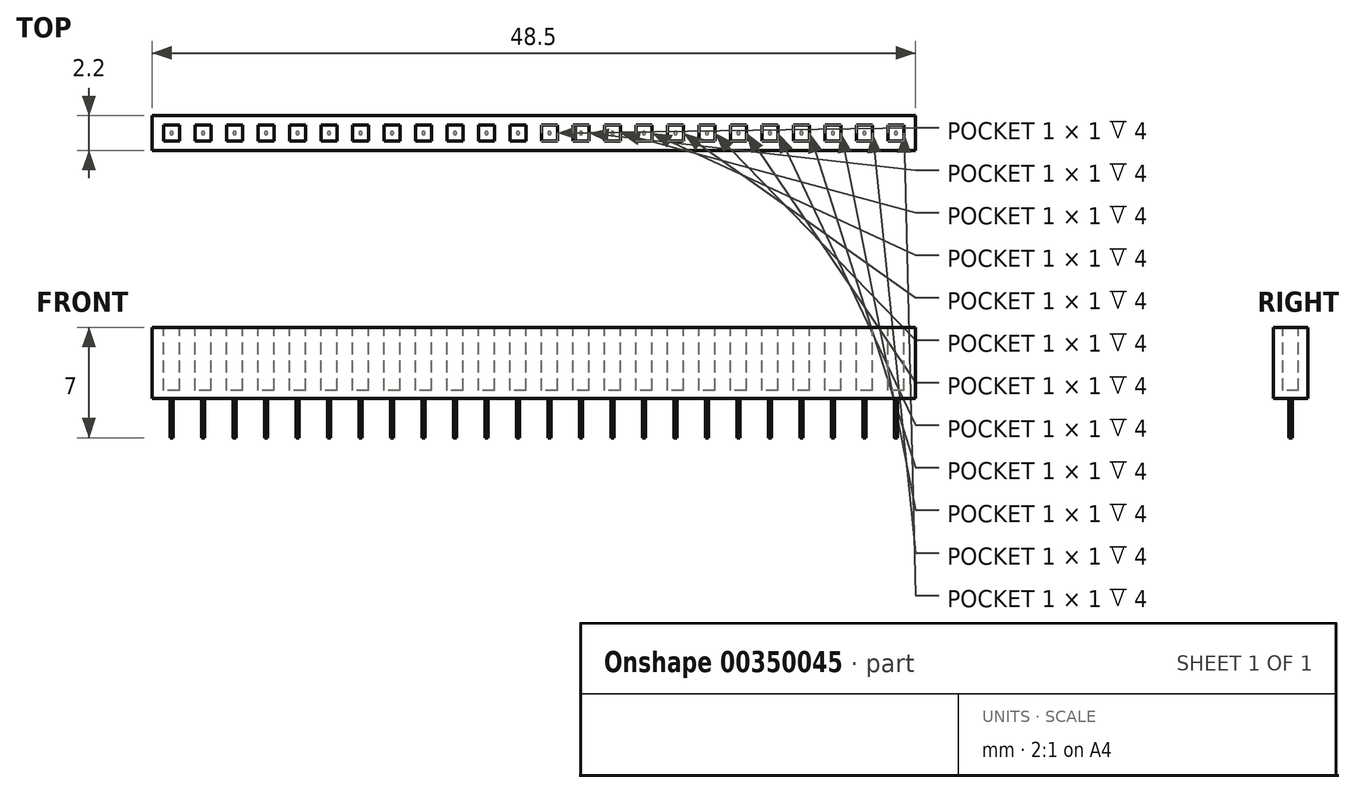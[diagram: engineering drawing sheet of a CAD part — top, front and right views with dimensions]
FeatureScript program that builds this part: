
annotation { "Feature Type Name" : "Feature", "Feature Type Description" : "" }
export const myFeature = defineFeature(function(context is Context, id is Id, definition is map)
    precondition{}
    {
        {
            var Q0;
            Q0=qCreatedBy(makeId("Top.planeOp"),FACE);
            var sketch = newSketch(context, id + "F0", { "sketchPlane" : qUnion([Q0])});
            skLineSegment(sketch, "E0.bottom", {"start": v(-24.25, 1.1) * mm, "end": v(24.25, 1.1) * mm});
            skLineSegment(sketch, "E0.top", {"start": v(-24.25, -1.1) * mm, "end": v(24.25, -1.1) * mm});
            skLineSegment(sketch, "E0.left", {"start": v(-24.25, 1.1) * mm, "end": v(-24.25, -1.1) * mm});
            skLineSegment(sketch, "E0.right", {"start": v(24.25, 1.1) * mm, "end": v(24.25, -1.1) * mm});
            skPoint(sketch, "E0.middle", {"position": v(0, 0) * mm});
            skSolve(sketch);
        }
        {
            var Q0;
            Q0=qSketchRegion(id+"F0",true);
            extrude(context, id + "F1", {"entities" : qUnion([Q0]), "depth" : 4.5 * mm});
        }
        {
            var Q0;
            Q0=makeQuery(id+"F1.opExtrude","CAP_FACE",FACE,{"disambiguationData":[OSD([sQuery(id+"F0.wireOp",EDGE,"E0.bottom"),sQuery(id+"F0.wireOp",EDGE,"E0.top"),sQuery(id+"F0.wireOp",EDGE,"E0.left"),sQuery(id+"F0.wireOp",EDGE,"E0.right")])],"isStart":false});
            var sketch = newSketch(context, id + "F2", { "sketchPlane" : qUnion([Q0])});
            skLineSegment(sketch, "E1.bottom", {"start": v(23.5, 0.5) * mm, "end": v(22.5, 0.5) * mm});
            skLineSegment(sketch, "E1.top", {"start": v(23.5, -0.5) * mm, "end": v(22.5, -0.5) * mm});
            skLineSegment(sketch, "E1.left", {"start": v(23.5, 0.5) * mm, "end": v(23.5, -0.5) * mm});
            skLineSegment(sketch, "E1.right", {"start": v(22.5, 0.5) * mm, "end": v(22.5, -0.5) * mm});
            skPoint(sketch, "E1.middle", {"position": v(23, 0) * mm});
            skLineSegment(sketch, "E2.1.0.0", {"start": v(21.5, 0.5) * mm, "end": v(20.5, 0.5) * mm});
            skLineSegment(sketch, "E2.1.0.1", {"start": v(21.5, -0.5) * mm, "end": v(20.5, -0.5) * mm});
            skLineSegment(sketch, "E2.1.0.2", {"start": v(21.5, 0.5) * mm, "end": v(21.5, -0.5) * mm});
            skLineSegment(sketch, "E2.1.0.3", {"start": v(20.5, 0.5) * mm, "end": v(20.5, -0.5) * mm});
            skLineSegment(sketch, "E2.2.0.0", {"start": v(19.5, 0.5) * mm, "end": v(18.5, 0.5) * mm});
            skLineSegment(sketch, "E2.2.0.1", {"start": v(19.5, -0.5) * mm, "end": v(18.5, -0.5) * mm});
            skLineSegment(sketch, "E2.2.0.2", {"start": v(19.5, 0.5) * mm, "end": v(19.5, -0.5) * mm});
            skLineSegment(sketch, "E2.2.0.3", {"start": v(18.5, 0.5) * mm, "end": v(18.5, -0.5) * mm});
            skLineSegment(sketch, "E2.3.0.0", {"start": v(17.5, 0.5) * mm, "end": v(16.5, 0.5) * mm});
            skLineSegment(sketch, "E2.3.0.1", {"start": v(17.5, -0.5) * mm, "end": v(16.5, -0.5) * mm});
            skLineSegment(sketch, "E2.3.0.2", {"start": v(17.5, 0.5) * mm, "end": v(17.5, -0.5) * mm});
            skLineSegment(sketch, "E2.3.0.3", {"start": v(16.5, 0.5) * mm, "end": v(16.5, -0.5) * mm});
            skLineSegment(sketch, "E2.4.0.0", {"start": v(15.5, 0.5) * mm, "end": v(14.5, 0.5) * mm});
            skLineSegment(sketch, "E2.4.0.1", {"start": v(15.5, -0.5) * mm, "end": v(14.5, -0.5) * mm});
            skLineSegment(sketch, "E2.4.0.2", {"start": v(15.5, 0.5) * mm, "end": v(15.5, -0.5) * mm});
            skLineSegment(sketch, "E2.4.0.3", {"start": v(14.5, 0.5) * mm, "end": v(14.5, -0.5) * mm});
            skLineSegment(sketch, "E2.5.0.0", {"start": v(13.5, 0.5) * mm, "end": v(12.5, 0.5) * mm});
            skLineSegment(sketch, "E2.5.0.1", {"start": v(13.5, -0.5) * mm, "end": v(12.5, -0.5) * mm});
            skLineSegment(sketch, "E2.5.0.2", {"start": v(13.5, 0.5) * mm, "end": v(13.5, -0.5) * mm});
            skLineSegment(sketch, "E2.5.0.3", {"start": v(12.5, 0.5) * mm, "end": v(12.5, -0.5) * mm});
            skLineSegment(sketch, "E2.6.0.0", {"start": v(11.5, 0.5) * mm, "end": v(10.5, 0.5) * mm});
            skLineSegment(sketch, "E2.6.0.1", {"start": v(11.5, -0.5) * mm, "end": v(10.5, -0.5) * mm});
            skLineSegment(sketch, "E2.6.0.2", {"start": v(11.5, 0.5) * mm, "end": v(11.5, -0.5) * mm});
            skLineSegment(sketch, "E2.6.0.3", {"start": v(10.5, 0.5) * mm, "end": v(10.5, -0.5) * mm});
            skLineSegment(sketch, "E2.7.0.0", {"start": v(9.5, 0.5) * mm, "end": v(8.5, 0.5) * mm});
            skLineSegment(sketch, "E2.7.0.1", {"start": v(9.5, -0.5) * mm, "end": v(8.5, -0.5) * mm});
            skLineSegment(sketch, "E2.7.0.2", {"start": v(9.5, 0.5) * mm, "end": v(9.5, -0.5) * mm});
            skLineSegment(sketch, "E2.7.0.3", {"start": v(8.5, 0.5) * mm, "end": v(8.5, -0.5) * mm});
            skLineSegment(sketch, "E2.8.0.0", {"start": v(7.5, 0.5) * mm, "end": v(6.5, 0.5) * mm});
            skLineSegment(sketch, "E2.8.0.1", {"start": v(7.5, -0.5) * mm, "end": v(6.5, -0.5) * mm});
            skLineSegment(sketch, "E2.8.0.2", {"start": v(7.5, 0.5) * mm, "end": v(7.5, -0.5) * mm});
            skLineSegment(sketch, "E2.8.0.3", {"start": v(6.5, 0.5) * mm, "end": v(6.5, -0.5) * mm});
            skLineSegment(sketch, "E2.9.0.0", {"start": v(5.5, 0.5) * mm, "end": v(4.5, 0.5) * mm});
            skLineSegment(sketch, "E2.9.0.1", {"start": v(5.5, -0.5) * mm, "end": v(4.5, -0.5) * mm});
            skLineSegment(sketch, "E2.9.0.2", {"start": v(5.5, 0.5) * mm, "end": v(5.5, -0.5) * mm});
            skLineSegment(sketch, "E2.9.0.3", {"start": v(4.5, 0.5) * mm, "end": v(4.5, -0.5) * mm});
            skLineSegment(sketch, "E2.10.0.0", {"start": v(3.5, 0.5) * mm, "end": v(2.5, 0.5) * mm});
            skLineSegment(sketch, "E2.10.0.1", {"start": v(3.5, -0.5) * mm, "end": v(2.5, -0.5) * mm});
            skLineSegment(sketch, "E2.10.0.2", {"start": v(3.5, 0.5) * mm, "end": v(3.5, -0.5) * mm});
            skLineSegment(sketch, "E2.10.0.3", {"start": v(2.5, 0.5) * mm, "end": v(2.5, -0.5) * mm});
            skLineSegment(sketch, "E2.11.0.0", {"start": v(1.5, 0.5) * mm, "end": v(0.5, 0.5) * mm});
            skLineSegment(sketch, "E2.11.0.1", {"start": v(1.5, -0.5) * mm, "end": v(0.5, -0.5) * mm});
            skLineSegment(sketch, "E2.11.0.2", {"start": v(1.5, 0.5) * mm, "end": v(1.5, -0.5) * mm});
            skLineSegment(sketch, "E2.11.0.3", {"start": v(0.5, 0.5) * mm, "end": v(0.5, -0.5) * mm});
            skLineSegment(sketch, "E2.12.0.0", {"start": v(-0.5, 0.5) * mm, "end": v(-1.5, 0.5) * mm});
            skLineSegment(sketch, "E2.12.0.1", {"start": v(-0.5, -0.5) * mm, "end": v(-1.5, -0.5) * mm});
            skLineSegment(sketch, "E2.12.0.2", {"start": v(-0.5, 0.5) * mm, "end": v(-0.5, -0.5) * mm});
            skLineSegment(sketch, "E2.12.0.3", {"start": v(-1.5, 0.5) * mm, "end": v(-1.5, -0.5) * mm});
            skLineSegment(sketch, "E2.13.0.0", {"start": v(-2.5, 0.5) * mm, "end": v(-3.5, 0.5) * mm});
            skLineSegment(sketch, "E2.13.0.1", {"start": v(-2.5, -0.5) * mm, "end": v(-3.5, -0.5) * mm});
            skLineSegment(sketch, "E2.13.0.2", {"start": v(-2.5, 0.5) * mm, "end": v(-2.5, -0.5) * mm});
            skLineSegment(sketch, "E2.13.0.3", {"start": v(-3.5, 0.5) * mm, "end": v(-3.5, -0.5) * mm});
            skLineSegment(sketch, "E2.14.0.0", {"start": v(-4.5, 0.5) * mm, "end": v(-5.5, 0.5) * mm});
            skLineSegment(sketch, "E2.14.0.1", {"start": v(-4.5, -0.5) * mm, "end": v(-5.5, -0.5) * mm});
            skLineSegment(sketch, "E2.14.0.2", {"start": v(-4.5, 0.5) * mm, "end": v(-4.5, -0.5) * mm});
            skLineSegment(sketch, "E2.14.0.3", {"start": v(-5.5, 0.5) * mm, "end": v(-5.5, -0.5) * mm});
            skLineSegment(sketch, "E2.15.0.0", {"start": v(-6.5, 0.5) * mm, "end": v(-7.5, 0.5) * mm});
            skLineSegment(sketch, "E2.15.0.1", {"start": v(-6.5, -0.5) * mm, "end": v(-7.5, -0.5) * mm});
            skLineSegment(sketch, "E2.15.0.2", {"start": v(-6.5, 0.5) * mm, "end": v(-6.5, -0.5) * mm});
            skLineSegment(sketch, "E2.15.0.3", {"start": v(-7.5, 0.5) * mm, "end": v(-7.5, -0.5) * mm});
            skLineSegment(sketch, "E2.16.0.0", {"start": v(-8.5, 0.5) * mm, "end": v(-9.5, 0.5) * mm});
            skLineSegment(sketch, "E2.16.0.1", {"start": v(-8.5, -0.5) * mm, "end": v(-9.5, -0.5) * mm});
            skLineSegment(sketch, "E2.16.0.2", {"start": v(-8.5, 0.5) * mm, "end": v(-8.5, -0.5) * mm});
            skLineSegment(sketch, "E2.16.0.3", {"start": v(-9.5, 0.5) * mm, "end": v(-9.5, -0.5) * mm});
            skLineSegment(sketch, "E2.17.0.0", {"start": v(-10.5, 0.5) * mm, "end": v(-11.5, 0.5) * mm});
            skLineSegment(sketch, "E2.17.0.1", {"start": v(-10.5, -0.5) * mm, "end": v(-11.5, -0.5) * mm});
            skLineSegment(sketch, "E2.17.0.2", {"start": v(-10.5, 0.5) * mm, "end": v(-10.5, -0.5) * mm});
            skLineSegment(sketch, "E2.17.0.3", {"start": v(-11.5, 0.5) * mm, "end": v(-11.5, -0.5) * mm});
            skLineSegment(sketch, "E2.18.0.0", {"start": v(-12.5, 0.5) * mm, "end": v(-13.5, 0.5) * mm});
            skLineSegment(sketch, "E2.18.0.1", {"start": v(-12.5, -0.5) * mm, "end": v(-13.5, -0.5) * mm});
            skLineSegment(sketch, "E2.18.0.2", {"start": v(-12.5, 0.5) * mm, "end": v(-12.5, -0.5) * mm});
            skLineSegment(sketch, "E2.18.0.3", {"start": v(-13.5, 0.5) * mm, "end": v(-13.5, -0.5) * mm});
            skLineSegment(sketch, "E2.19.0.0", {"start": v(-14.5, 0.5) * mm, "end": v(-15.5, 0.5) * mm});
            skLineSegment(sketch, "E2.19.0.1", {"start": v(-14.5, -0.5) * mm, "end": v(-15.5, -0.5) * mm});
            skLineSegment(sketch, "E2.19.0.2", {"start": v(-14.5, 0.5) * mm, "end": v(-14.5, -0.5) * mm});
            skLineSegment(sketch, "E2.19.0.3", {"start": v(-15.5, 0.5) * mm, "end": v(-15.5, -0.5) * mm});
            skLineSegment(sketch, "E2.20.0.0", {"start": v(-16.5, 0.5) * mm, "end": v(-17.5, 0.5) * mm});
            skLineSegment(sketch, "E2.20.0.1", {"start": v(-16.5, -0.5) * mm, "end": v(-17.5, -0.5) * mm});
            skLineSegment(sketch, "E2.20.0.2", {"start": v(-16.5, 0.5) * mm, "end": v(-16.5, -0.5) * mm});
            skLineSegment(sketch, "E2.20.0.3", {"start": v(-17.5, 0.5) * mm, "end": v(-17.5, -0.5) * mm});
            skLineSegment(sketch, "E2.21.0.0", {"start": v(-18.5, 0.5) * mm, "end": v(-19.5, 0.5) * mm});
            skLineSegment(sketch, "E2.21.0.1", {"start": v(-18.5, -0.5) * mm, "end": v(-19.5, -0.5) * mm});
            skLineSegment(sketch, "E2.21.0.2", {"start": v(-18.5, 0.5) * mm, "end": v(-18.5, -0.5) * mm});
            skLineSegment(sketch, "E2.21.0.3", {"start": v(-19.5, 0.5) * mm, "end": v(-19.5, -0.5) * mm});
            skLineSegment(sketch, "E2.22.0.0", {"start": v(-20.5, 0.5) * mm, "end": v(-21.5, 0.5) * mm});
            skLineSegment(sketch, "E2.22.0.1", {"start": v(-20.5, -0.5) * mm, "end": v(-21.5, -0.5) * mm});
            skLineSegment(sketch, "E2.22.0.2", {"start": v(-20.5, 0.5) * mm, "end": v(-20.5, -0.5) * mm});
            skLineSegment(sketch, "E2.22.0.3", {"start": v(-21.5, 0.5) * mm, "end": v(-21.5, -0.5) * mm});
            skLineSegment(sketch, "E2.23.0.0", {"start": v(-22.5, 0.5) * mm, "end": v(-23.5, 0.5) * mm});
            skLineSegment(sketch, "E2.23.0.1", {"start": v(-22.5, -0.5) * mm, "end": v(-23.5, -0.5) * mm});
            skLineSegment(sketch, "E2.23.0.2", {"start": v(-22.5, 0.5) * mm, "end": v(-22.5, -0.5) * mm});
            skLineSegment(sketch, "E2.23.0.3", {"start": v(-23.5, 0.5) * mm, "end": v(-23.5, -0.5) * mm});
            skLineSegment(sketch, "E2.direction1", {"start": v(22.5, 0.5) * mm, "end": v(20.5, 0.5) * mm, "construction": true});
            skSolve(sketch);
        }
        {
            var Q0;
            Q0=qSketchRegion(id+"F2",true);
            extrude(context, id + "F3", {"entities" : qUnion([Q0]), "operationType" : NewBodyOperationType.REMOVE, "oppositeDirection" : true, "depth" : 4 * mm});
        }
        {
            var Q0;
            Q0=makeQuery(id+"F1.opExtrude","CAP_FACE",FACE,{"disambiguationData":[OSD([sQuery(id+"F0.wireOp",EDGE,"E0.bottom"),sQuery(id+"F0.wireOp",EDGE,"E0.top"),sQuery(id+"F0.wireOp",EDGE,"E0.left"),sQuery(id+"F0.wireOp",EDGE,"E0.right")])],"isStart":true});
            var sketch = newSketch(context, id + "F4", { "sketchPlane" : qUnion([Q0])});
            skCircle(sketch, "E3", {"center": v(23, 0) * mm, "radius": 0.1 * mm});
            skCircle(sketch, "E4.1.0.0", {"center": v(21, 0) * mm, "radius": 0.1 * mm});
            skCircle(sketch, "E4.2.0.0", {"center": v(19, 0) * mm, "radius": 0.1 * mm});
            skCircle(sketch, "E4.3.0.0", {"center": v(17, 0) * mm, "radius": 0.1 * mm});
            skCircle(sketch, "E4.4.0.0", {"center": v(15, 0) * mm, "radius": 0.1 * mm});
            skCircle(sketch, "E4.5.0.0", {"center": v(13, 0) * mm, "radius": 0.1 * mm});
            skCircle(sketch, "E4.6.0.0", {"center": v(11, 0) * mm, "radius": 0.1 * mm});
            skCircle(sketch, "E4.7.0.0", {"center": v(9, 0) * mm, "radius": 0.1 * mm});
            skCircle(sketch, "E4.8.0.0", {"center": v(7, 0) * mm, "radius": 0.1 * mm});
            skCircle(sketch, "E4.9.0.0", {"center": v(5, 0) * mm, "radius": 0.1 * mm});
            skCircle(sketch, "E4.10.0.0", {"center": v(3, 0) * mm, "radius": 0.1 * mm});
            skCircle(sketch, "E4.11.0.0", {"center": v(1, 0) * mm, "radius": 0.1 * mm});
            skCircle(sketch, "E4.12.0.0", {"center": v(-1, 0) * mm, "radius": 0.1 * mm});
            skCircle(sketch, "E4.13.0.0", {"center": v(-3, 0) * mm, "radius": 0.1 * mm});
            skCircle(sketch, "E4.14.0.0", {"center": v(-5, 0) * mm, "radius": 0.1 * mm});
            skCircle(sketch, "E4.15.0.0", {"center": v(-7, 0) * mm, "radius": 0.1 * mm});
            skCircle(sketch, "E4.16.0.0", {"center": v(-9, 0) * mm, "radius": 0.1 * mm});
            skCircle(sketch, "E4.17.0.0", {"center": v(-11, 0) * mm, "radius": 0.1 * mm});
            skCircle(sketch, "E4.18.0.0", {"center": v(-13, 0) * mm, "radius": 0.1 * mm});
            skCircle(sketch, "E4.19.0.0", {"center": v(-15, 0) * mm, "radius": 0.1 * mm});
            skCircle(sketch, "E4.20.0.0", {"center": v(-17, 0) * mm, "radius": 0.1 * mm});
            skCircle(sketch, "E4.21.0.0", {"center": v(-19, 0) * mm, "radius": 0.1 * mm});
            skCircle(sketch, "E4.22.0.0", {"center": v(-21, 0) * mm, "radius": 0.1 * mm});
            skCircle(sketch, "E4.23.0.0", {"center": v(-23, 0) * mm, "radius": 0.1 * mm});
            skLineSegment(sketch, "E4.direction1", {"start": v(23, 0) * mm, "end": v(21, 0) * mm, "construction": true});
            skSolve(sketch);
        }
        {
            var Q0;
            Q0=qSketchRegion(id+"F4",true);
            extrude(context, id + "F5", {"entities" : qUnion([Q0]), "operationType" : NewBodyOperationType.ADD, "depth" : 2.5 * mm});
        }
    });
